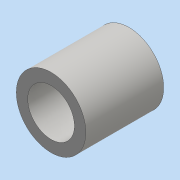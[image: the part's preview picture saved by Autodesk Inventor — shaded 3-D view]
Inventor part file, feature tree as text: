
AUTODESK INVENTOR PART (.ipt)
format: ipt  version: 2016 (Build 200138000, 138)  size: 79,872 bytes
history: native  units: mm
features: extrude x1, sketch x1
ambient origin geometry x8: Origin, YZ Plane, XZ Plane, XY Plane, X Axis, Y Axis, Z Axis, Center Point
bodies: Solid1 (feature_tree)
feature tree (2):
  extrude  "Extrusion1"  Depth=5.0mm
  sketch  "Sketch1"  dims[d0=3.0mm d1=0.736068mm d2=5.0mm d3=0.0mm]
